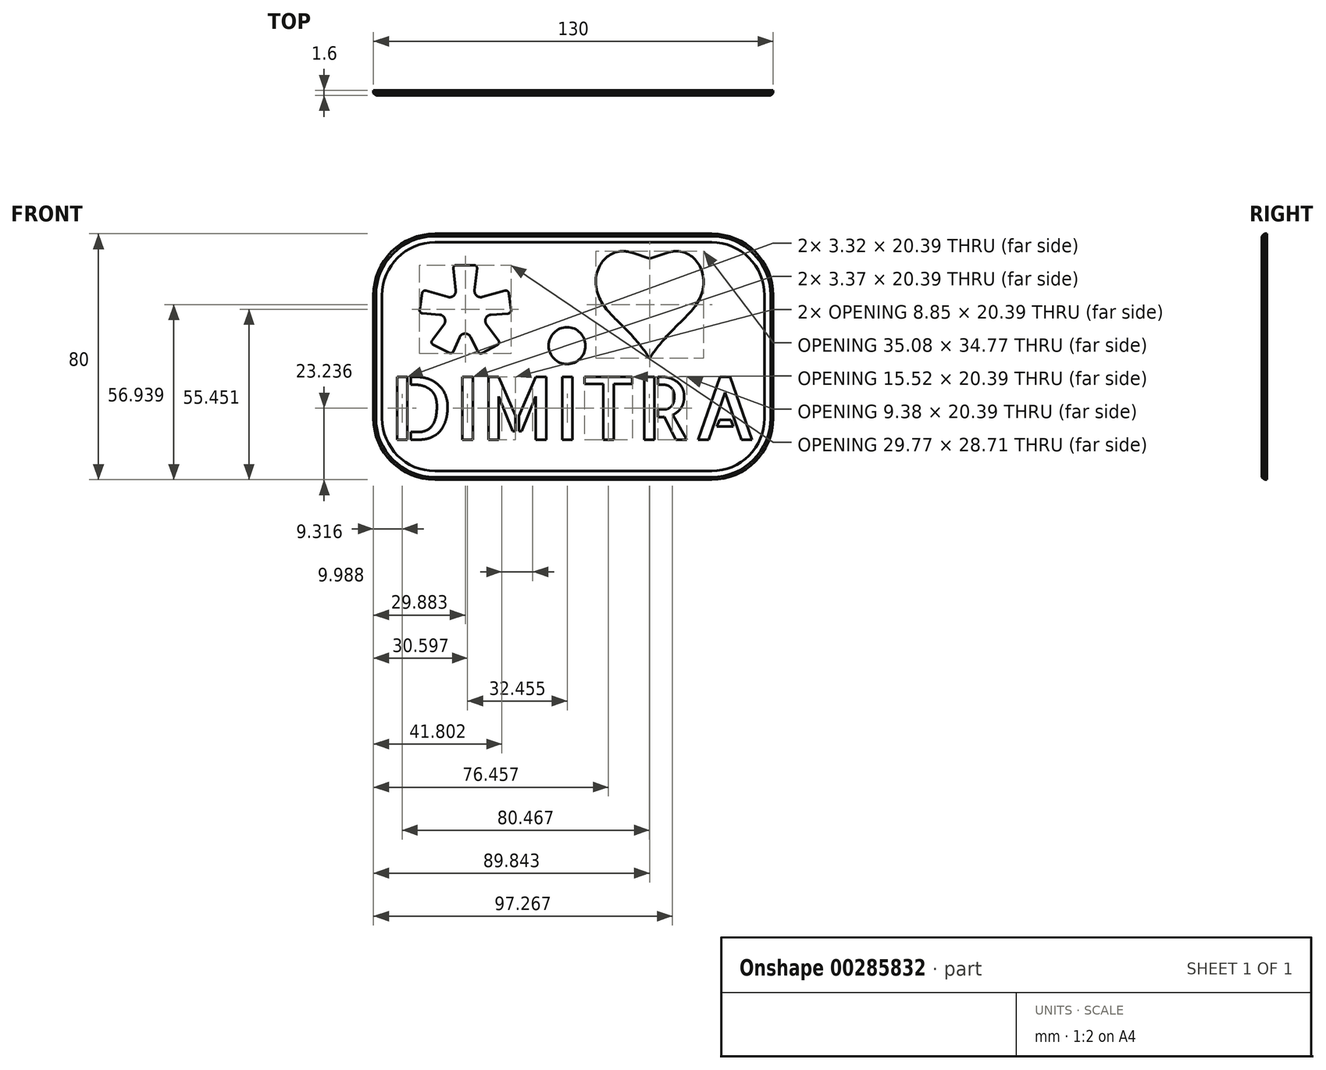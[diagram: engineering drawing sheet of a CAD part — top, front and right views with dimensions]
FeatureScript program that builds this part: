
annotation { "Feature Type Name" : "Feature", "Feature Type Description" : "" }
export const myFeature = defineFeature(function(context is Context, id is Id, definition is map)
    precondition{}
    {
        {
            var Q0;
            Q0=qCreatedBy(makeId("Front.planeOp"),FACE);
            var sketch = newSketch(context, id + "F0", { "sketchPlane" : qUnion([Q0])});
            skLineSegment(sketch, "E0.bottom", {"start": v(-65, 60) * mm, "end": v(65, 60) * mm});
            skLineSegment(sketch, "E0.top", {"start": v(-65, -20) * mm, "end": v(65, -20) * mm});
            skLineSegment(sketch, "E0.left", {"start": v(-65, 60) * mm, "end": v(-65, -20) * mm});
            skLineSegment(sketch, "E0.right", {"start": v(65, 60) * mm, "end": v(65, -20) * mm});
            skSolve(sketch);
        }
        {
            var Q0;
            Q0=qSketchRegion(id+"F0",true);
            extrude(context, id + "F1", {"entities" : qUnion([Q0]), "depth" : 1.6 * mm});
        }
        {
            var Q0;
            Q0=makeQuery(id+"F1.opExtrude","CAP_FACE",FACE,{"disambiguationData":[OSD([sQuery(id+"F0.wireOp",EDGE,"E0.bottom"),sQuery(id+"F0.wireOp",EDGE,"E0.top"),sQuery(id+"F0.wireOp",EDGE,"E0.left"),sQuery(id+"F0.wireOp",EDGE,"E0.right")])],"isStart":false});
            var sketch = newSketch(context, id + "F2", { "sketchPlane" : qUnion([Q0])});
            skText(sketch, "E1", { "text": "DIMITRA", "fontName": "AllertaStencil-Regular.ttf"});
            skText(sketch, "E2", { "text": "♥", "fontName": "NotoSansCJKjp-Regular.otf"});
            skCircle(sketch, "E3", {"center": v(-2.04, 23.59) * mm, "radius": 6 * mm});
            const initialGuessF2  = {"E1": [-0.06, -0.00696, 1, 0, 0.0204], "E2": [0.00401, 0.02116, 1, 0, 0.03]};
            skSetInitialGuess(sketch, initialGuessF2);
            skSolve(sketch);
        }
        {
            var Q0;
            Q0=qSketchRegion(id+"F2",true);
            extrude(context, id + "F3", {"entities" : qUnion([Q0]), "operationType" : NewBodyOperationType.REMOVE, "endBound" : BoundingType.THROUGH_ALL, "oppositeDirection" : true, "depth" : 25 * mm});
        }
        {
            var Q0;
            Q0=makeQuery(id+"F1.opExtrude","SWEPT_EDGE",EDGE,{"disambiguationData":[OSD([sQuery(id+"F0.wireOp",EDGE,"E0.top"),sQuery(id+"F0.wireOp",EDGE,"E0.right")])]});
            var Q1;
            Q1=makeQuery(id+"F1.opExtrude","SWEPT_EDGE",EDGE,{"disambiguationData":[OSD([sQuery(id+"F0.wireOp",EDGE,"E0.bottom"),sQuery(id+"F0.wireOp",EDGE,"E0.right")])]});
            var Q2;
            Q2=makeQuery(id+"F1.opExtrude","SWEPT_EDGE",EDGE,{"disambiguationData":[OSD([sQuery(id+"F0.wireOp",EDGE,"E0.top"),sQuery(id+"F0.wireOp",EDGE,"E0.left")])]});
            var Q3;
            Q3=makeQuery(id+"F1.opExtrude","SWEPT_EDGE",EDGE,{"disambiguationData":[OSD([sQuery(id+"F0.wireOp",EDGE,"E0.bottom"),sQuery(id+"F0.wireOp",EDGE,"E0.left")])]});
            fillet(context, id + "F4", {"entities" : qUnion([Q0, Q1, Q2, Q3]), "radius" : 20 * mm, "tangentPropagation" : true, "allowEdgeOverflow" : false});
        }
        {
            var Q0;
            Q0=makeQuery(id+"F1.opExtrude","CAP_EDGE",EDGE,{"disambiguationData":[OSD([sQuery(id+"F0.wireOp",EDGE,"E0.top")])],"isStart":false});
            chamfer(context, id + "F5", {"entities" : qUnion([Q0]), "width" : 0.8 * mm, "tangentPropagation" : true});
        }
        {
            var Q0;
            Q0=makeQuery(id+"F1.opExtrude","CAP_FACE",FACE,{"disambiguationData":[OSD([sQuery(id+"F0.wireOp",EDGE,"E0.bottom"),sQuery(id+"F0.wireOp",EDGE,"E0.top"),sQuery(id+"F0.wireOp",EDGE,"E0.left"),sQuery(id+"F0.wireOp",EDGE,"E0.right")])],"isStart":false});
            var sketch = newSketch(context, id + "F6", { "sketchPlane" : qUnion([Q0])});
            skText(sketch, "E4", { "text": "*", "fontName": "OpenSans-Bold.ttf"});
            const initialGuessF6  = {"E4": [-0.05207, 0.00257, 1, 0, 0.04476]};
            skSetInitialGuess(sketch, initialGuessF6);
            skSolve(sketch);
        }
        {
            var Q0;
            Q0=qSketchRegion(id+"F6",true);
            extrude(context, id + "F7", {"entities" : qUnion([Q0]), "operationType" : NewBodyOperationType.REMOVE, "endBound" : BoundingType.THROUGH_ALL, "oppositeDirection" : true, "depth" : 25 * mm});
        }
        {
            var Q0;
            Q0=makeQuery(id+"F1.opExtrude","CAP_FACE",FACE,{"disambiguationData":[OSD([sQuery(id+"F0.wireOp",EDGE,"E0.bottom"),sQuery(id+"F0.wireOp",EDGE,"E0.top"),sQuery(id+"F0.wireOp",EDGE,"E0.left"),sQuery(id+"F0.wireOp",EDGE,"E0.right")])],"isStart":false});
            var sketch = newSketch(context, id + "F8", { "sketchPlane" : qUnion([Q0])});
            skLineSegment(sketch, "E5.0", {"start": v(62.2, 0) * mm, "end": v(62.2, 40) * mm});
            skArc(sketch, "E5.1", {"start": v(45, -17.2) * mm, "mid": v(57.16, -12.16) * mm, "end": v(62.2, 0) * mm});
            skLineSegment(sketch, "E5.2", {"start": v(-45, -17.2) * mm, "end": v(45, -17.2) * mm});
            skArc(sketch, "E6.0", {"start": v(-62.2, 0) * mm, "mid": v(-57.16, -12.16) * mm, "end": v(-45, -17.2) * mm});
            skArc(sketch, "E6.1", {"start": v(62.2, 40) * mm, "mid": v(57.16, 52.16) * mm, "end": v(45, 57.2) * mm});
            skLineSegment(sketch, "E6.2", {"start": v(45, 57.2) * mm, "end": v(-45, 57.2) * mm});
            skArc(sketch, "E6.3", {"start": v(-45, 57.2) * mm, "mid": v(-57.16, 52.16) * mm, "end": v(-62.2, 40) * mm});
            skLineSegment(sketch, "E6.4", {"start": v(-62.2, 40) * mm, "end": v(-62.2, 0) * mm});
            skSolve(sketch);
        }
        {
            var Q0;
            Q0=makeQuery(id+"F8.imprint","IMPRINT",FACE,{"disambiguationData":[TD([[makeQuery(id+"F8.imprint","IMPRINT",EDGE,{"derivedFrom":sQuery(id+"F8.wireOp",EDGE,"E5.0")}),1.0]])]});
            extrude(context, id + "F9", {"entities" : qUnion([Q0]), "operationType" : NewBodyOperationType.REMOVE, "oppositeDirection" : true, "depth" : 0.4 * mm});
        }
        {
            var Q0;
            Q0=makeQuery(id+"F9.boolean.opBoolean","COPY",FACE,{"derivedFrom":makeQuery(id+"F9.opExtrude","CAP_FACE",FACE,{"disambiguationData":[OSD([sQuery(id+"F2.wireOp",EDGE,"E1.sketch_text.stroke-0"),sQuery(id+"F2.wireOp",EDGE,"E1.sketch_text.stroke-1"),sQuery(id+"F2.wireOp",EDGE,"E1.sketch_text.stroke-2"),sQuery(id+"F2.wireOp",EDGE,"E1.sketch_text.stroke-3"),sQuery(id+"F2.wireOp",EDGE,"E1.sketch_text.stroke-4"),sQuery(id+"F2.wireOp",EDGE,"E1.sketch_text.stroke-5"),sQuery(id+"F2.wireOp",EDGE,"E1.sketch_text.stroke-6"),sQuery(id+"F2.wireOp",EDGE,"E1.sketch_text.stroke-7"),sQuery(id+"F2.wireOp",EDGE,"E1.sketch_text.stroke-8"),sQuery(id+"F2.wireOp",EDGE,"E1.sketch_text.stroke-9"),sQuery(id+"F2.wireOp",EDGE,"E1.sketch_text.stroke-10"),sQuery(id+"F2.wireOp",EDGE,"E1.sketch_text.stroke-11"),sQuery(id+"F2.wireOp",EDGE,"E1.sketch_text.stroke-12"),sQuery(id+"F2.wireOp",EDGE,"E1.sketch_text.stroke-13"),sQuery(id+"F2.wireOp",EDGE,"E1.sketch_text.stroke-14"),sQuery(id+"F2.wireOp",EDGE,"E1.sketch_text.stroke-15"),sQuery(id+"F2.wireOp",EDGE,"E1.sketch_text.stroke-16"),sQuery(id+"F2.wireOp",EDGE,"E1.sketch_text.stroke-17"),sQuery(id+"F2.wireOp",EDGE,"E1.sketch_text.stroke-18"),sQuery(id+"F2.wireOp",EDGE,"E1.sketch_text.stroke-19"),sQuery(id+"F2.wireOp",EDGE,"E1.sketch_text.stroke-20"),sQuery(id+"F2.wireOp",EDGE,"E1.sketch_text.stroke-21"),sQuery(id+"F2.wireOp",EDGE,"E1.sketch_text.stroke-22"),sQuery(id+"F2.wireOp",EDGE,"E1.sketch_text.stroke-23"),sQuery(id+"F2.wireOp",EDGE,"E1.sketch_text.stroke-24"),sQuery(id+"F2.wireOp",EDGE,"E1.sketch_text.stroke-25"),sQuery(id+"F2.wireOp",EDGE,"E1.sketch_text.stroke-26"),sQuery(id+"F2.wireOp",EDGE,"E1.sketch_text.stroke-27"),sQuery(id+"F2.wireOp",EDGE,"E1.sketch_text.stroke-28"),sQuery(id+"F2.wireOp",EDGE,"E1.sketch_text.stroke-29"),sQuery(id+"F2.wireOp",EDGE,"E1.sketch_text.stroke-30"),sQuery(id+"F2.wireOp",EDGE,"E1.sketch_text.stroke-31"),sQuery(id+"F2.wireOp",EDGE,"E1.sketch_text.stroke-32"),sQuery(id+"F2.wireOp",EDGE,"E1.sketch_text.stroke-33"),sQuery(id+"F2.wireOp",EDGE,"E1.sketch_text.stroke-34"),sQuery(id+"F2.wireOp",EDGE,"E1.sketch_text.stroke-35"),sQuery(id+"F2.wireOp",EDGE,"E1.sketch_text.stroke-36"),sQuery(id+"F2.wireOp",EDGE,"E1.sketch_text.stroke-37"),sQuery(id+"F2.wireOp",EDGE,"E1.sketch_text.stroke-38"),sQuery(id+"F2.wireOp",EDGE,"E1.sketch_text.stroke-39"),sQuery(id+"F2.wireOp",EDGE,"E1.sketch_text.stroke-40"),sQuery(id+"F2.wireOp",EDGE,"E1.sketch_text.stroke-41"),sQuery(id+"F2.wireOp",EDGE,"E1.sketch_text.stroke-42"),sQuery(id+"F2.wireOp",EDGE,"E1.sketch_text.stroke-43"),sQuery(id+"F2.wireOp",EDGE,"E1.sketch_text.stroke-44"),sQuery(id+"F2.wireOp",EDGE,"E1.sketch_text.stroke-45"),sQuery(id+"F2.wireOp",EDGE,"E1.sketch_text.stroke-46"),sQuery(id+"F2.wireOp",EDGE,"E1.sketch_text.stroke-47"),sQuery(id+"F2.wireOp",EDGE,"E1.sketch_text.stroke-48"),sQuery(id+"F2.wireOp",EDGE,"E1.sketch_text.stroke-49"),sQuery(id+"F2.wireOp",EDGE,"E1.sketch_text.stroke-50"),sQuery(id+"F2.wireOp",EDGE,"E1.sketch_text.stroke-51"),sQuery(id+"F2.wireOp",EDGE,"E1.sketch_text.stroke-52"),sQuery(id+"F2.wireOp",EDGE,"E1.sketch_text.stroke-53"),sQuery(id+"F2.wireOp",EDGE,"E1.sketch_text.stroke-54"),sQuery(id+"F2.wireOp",EDGE,"E1.sketch_text.stroke-55"),sQuery(id+"F2.wireOp",EDGE,"E1.sketch_text.stroke-56"),sQuery(id+"F2.wireOp",EDGE,"E1.sketch_text.stroke-57"),sQuery(id+"F2.wireOp",EDGE,"E1.sketch_text.stroke-58"),sQuery(id+"F2.wireOp",EDGE,"E1.sketch_text.stroke-59"),sQuery(id+"F2.wireOp",EDGE,"E1.sketch_text.stroke-60"),sQuery(id+"F2.wireOp",EDGE,"E1.sketch_text.stroke-61"),sQuery(id+"F2.wireOp",EDGE,"E1.sketch_text.stroke-62"),sQuery(id+"F2.wireOp",EDGE,"E1.sketch_text.stroke-63"),sQuery(id+"F2.wireOp",EDGE,"E1.sketch_text.stroke-64"),sQuery(id+"F2.wireOp",EDGE,"E1.sketch_text.stroke-65"),sQuery(id+"F2.wireOp",EDGE,"E1.sketch_text.stroke-66"),sQuery(id+"F2.wireOp",EDGE,"E1.sketch_text.stroke-67"),sQuery(id+"F2.wireOp",EDGE,"E1.sketch_text.stroke-68"),sQuery(id+"F2.wireOp",EDGE,"E1.sketch_text.stroke-69"),sQuery(id+"F2.wireOp",EDGE,"E1.sketch_text.stroke-70"),sQuery(id+"F2.wireOp",EDGE,"E1.sketch_text.stroke-71"),sQuery(id+"F2.wireOp",EDGE,"E1.sketch_text.stroke-72"),sQuery(id+"F2.wireOp",EDGE,"E1.sketch_text.stroke-73"),sQuery(id+"F2.wireOp",EDGE,"E1.sketch_text.stroke-74"),sQuery(id+"F2.wireOp",EDGE,"E1.sketch_text.stroke-75"),sQuery(id+"F2.wireOp",EDGE,"E1.sketch_text.stroke-76"),sQuery(id+"F2.wireOp",EDGE,"E1.sketch_text.stroke-77"),sQuery(id+"F2.wireOp",EDGE,"E1.sketch_text.stroke-78"),sQuery(id+"F2.wireOp",EDGE,"E1.sketch_text.stroke-79"),sQuery(id+"F2.wireOp",EDGE,"E1.sketch_text.stroke-80"),sQuery(id+"F2.wireOp",EDGE,"E1.sketch_text.stroke-81"),sQuery(id+"F2.wireOp",EDGE,"E1.sketch_text.stroke-82"),sQuery(id+"F2.wireOp",EDGE,"E1.sketch_text.stroke-83"),sQuery(id+"F2.wireOp",EDGE,"E1.sketch_text.stroke-84"),sQuery(id+"F2.wireOp",EDGE,"E1.sketch_text.stroke-85"),sQuery(id+"F2.wireOp",EDGE,"E1.sketch_text.stroke-86"),sQuery(id+"F2.wireOp",EDGE,"E1.sketch_text.stroke-87"),sQuery(id+"F2.wireOp",EDGE,"E1.sketch_text.stroke-88"),sQuery(id+"F2.wireOp",EDGE,"E1.sketch_text.stroke-89"),sQuery(id+"F2.wireOp",EDGE,"E1.sketch_text.stroke-90"),sQuery(id+"F2.wireOp",EDGE,"E1.sketch_text.stroke-91"),sQuery(id+"F2.wireOp",EDGE,"E1.sketch_text.stroke-92"),sQuery(id+"F2.wireOp",EDGE,"E1.sketch_text.stroke-93"),sQuery(id+"F2.wireOp",EDGE,"E1.sketch_text.stroke-94"),sQuery(id+"F2.wireOp",EDGE,"E1.sketch_text.stroke-95"),sQuery(id+"F2.wireOp",EDGE,"E1.sketch_text.stroke-96"),sQuery(id+"F2.wireOp",EDGE,"E1.sketch_text.stroke-97"),sQuery(id+"F2.wireOp",EDGE,"E1.sketch_text.stroke-98"),sQuery(id+"F2.wireOp",EDGE,"E2.sketch_text.stroke-0"),sQuery(id+"F2.wireOp",EDGE,"E2.sketch_text.stroke-1"),sQuery(id+"F2.wireOp",EDGE,"E2.sketch_text.stroke-2"),sQuery(id+"F2.wireOp",EDGE,"E2.sketch_text.stroke-3"),sQuery(id+"F2.wireOp",EDGE,"E2.sketch_text.stroke-4"),sQuery(id+"F2.wireOp",EDGE,"E2.sketch_text.stroke-5"),sQuery(id+"F2.wireOp",EDGE,"E2.sketch_text.stroke-6"),sQuery(id+"F2.wireOp",EDGE,"E2.sketch_text.stroke-7"),sQuery(id+"F2.wireOp",EDGE,"E2.sketch_text.stroke-8"),sQuery(id+"F2.wireOp",EDGE,"E2.sketch_text.stroke-9"),sQuery(id+"F2.wireOp",EDGE,"E2.sketch_text.stroke-10"),sQuery(id+"F6.wireOp",EDGE,"E4.sketch_text.stroke-0"),sQuery(id+"F6.wireOp",EDGE,"E4.sketch_text.stroke-1"),sQuery(id+"F6.wireOp",EDGE,"E4.sketch_text.stroke-2"),sQuery(id+"F6.wireOp",EDGE,"E4.sketch_text.stroke-3"),sQuery(id+"F6.wireOp",EDGE,"E4.sketch_text.stroke-4"),sQuery(id+"F6.wireOp",EDGE,"E4.sketch_text.stroke-5"),sQuery(id+"F6.wireOp",EDGE,"E4.sketch_text.stroke-6"),sQuery(id+"F6.wireOp",EDGE,"E4.sketch_text.stroke-7"),sQuery(id+"F6.wireOp",EDGE,"E4.sketch_text.stroke-8"),sQuery(id+"F6.wireOp",EDGE,"E4.sketch_text.stroke-9"),sQuery(id+"F6.wireOp",EDGE,"E4.sketch_text.stroke-10"),sQuery(id+"F6.wireOp",EDGE,"E4.sketch_text.stroke-11"),sQuery(id+"F6.wireOp",EDGE,"E4.sketch_text.stroke-12"),sQuery(id+"F6.wireOp",EDGE,"E4.sketch_text.stroke-13"),sQuery(id+"F6.wireOp",EDGE,"E4.sketch_text.stroke-14"),sQuery(id+"F6.wireOp",EDGE,"E4.sketch_text.stroke-15"),sQuery(id+"F6.wireOp",EDGE,"E4.sketch_text.stroke-16"),sQuery(id+"F6.wireOp",EDGE,"E4.sketch_text.stroke-17"),sQuery(id+"F6.wireOp",EDGE,"E4.sketch_text.stroke-18"),sQuery(id+"F6.wireOp",EDGE,"E4.sketch_text.stroke-19"),sQuery(id+"F6.wireOp",EDGE,"E4.sketch_text.stroke-20"),sQuery(id+"F6.wireOp",EDGE,"E4.sketch_text.stroke-21"),sQuery(id+"F6.wireOp",EDGE,"E4.sketch_text.stroke-22"),sQuery(id+"F6.wireOp",EDGE,"E4.sketch_text.stroke-23"),sQuery(id+"F6.wireOp",EDGE,"E4.sketch_text.stroke-24"),sQuery(id+"F6.wireOp",EDGE,"E4.sketch_text.stroke-25"),sQuery(id+"F6.wireOp",EDGE,"E4.sketch_text.stroke-26"),sQuery(id+"F6.wireOp",EDGE,"E4.sketch_text.stroke-27"),sQuery(id+"F6.wireOp",EDGE,"E4.sketch_text.stroke-28"),sQuery(id+"F6.wireOp",EDGE,"E4.sketch_text.stroke-29"),sQuery(id+"F6.wireOp",EDGE,"E4.sketch_text.stroke-30"),sQuery(id+"F6.wireOp",EDGE,"E4.sketch_text.stroke-31"),sQuery(id+"F6.wireOp",EDGE,"E4.sketch_text.stroke-32"),sQuery(id+"F6.wireOp",EDGE,"E4.sketch_text.stroke-33"),sQuery(id+"F8.wireOp",EDGE,"E5.0"),sQuery(id+"F8.wireOp",EDGE,"E5.1"),sQuery(id+"F8.wireOp",EDGE,"E5.2"),sQuery(id+"F8.wireOp",EDGE,"E6.0"),sQuery(id+"F8.wireOp",EDGE,"E6.1"),sQuery(id+"F8.wireOp",EDGE,"E6.2"),sQuery(id+"F8.wireOp",EDGE,"E6.3"),sQuery(id+"F8.wireOp",EDGE,"E6.4")])],"isStart":false})});
            var sketch = newSketch(context, id + "F10", { "sketchPlane" : qUnion([Q0])});
            skLineSegment(sketch, "E7", {"start": v(20.28, 45.7) * mm, "end": v(30.45, 45.7) * mm});
            skLineSegment(sketch, "E8", {"start": v(30.45, 45.7) * mm, "end": v(30.45, 53.8) * mm});
            skLineSegment(sketch, "E9", {"start": v(30.45, 53.8) * mm, "end": v(24.85, 51.87) * mm});
            skLineSegment(sketch, "E10", {"start": v(24.85, 51.87) * mm, "end": v(19.22, 53.8) * mm});
            skLineSegment(sketch, "E11", {"start": v(19.22, 53.8) * mm, "end": v(19.22, 45.6) * mm});
            skLineSegment(sketch, "E12", {"start": v(19.22, 45.6) * mm, "end": v(20.28, 45.7) * mm});
            skSolve(sketch);
        }
        {
            var Q0;
            Q0 = qSketchRegion(id + "F10", true);
            extrude(context, id + "F11", {"entities" : qUnion([Q0]), "operationType" : NewBodyOperationType.REMOVE, "oppositeDirection" : true, "depth" : 25 * mm});
        }
        {
            var Q0;
            Q0=makeQuery(id+"F7.boolean.opBoolean","COPY",EDGE,{"derivedFrom":makeQuery(id+"F7.opExtrude","SWEPT_EDGE",EDGE,{"disambiguationData":[OSD([sQuery(id+"F6.wireOp",EDGE,"E4.sketch_text.stroke-6"),sQuery(id+"F6.wireOp",EDGE,"E4.sketch_text.stroke-7")])]})});
            var Q1;
            Q1=makeQuery(id+"F7.boolean.opBoolean","COPY",EDGE,{"derivedFrom":makeQuery(id+"F7.opExtrude","SWEPT_EDGE",EDGE,{"disambiguationData":[OSD([sQuery(id+"F6.wireOp",EDGE,"E4.sketch_text.stroke-9"),sQuery(id+"F6.wireOp",EDGE,"E4.sketch_text.stroke-10")])]})});
            var Q2;
            Q2=makeQuery(id+"F7.boolean.opBoolean","COPY",EDGE,{"derivedFrom":makeQuery(id+"F7.opExtrude","SWEPT_EDGE",EDGE,{"disambiguationData":[OSD([sQuery(id+"F6.wireOp",EDGE,"E4.sketch_text.stroke-3"),sQuery(id+"F6.wireOp",EDGE,"E4.sketch_text.stroke-4")])]})});
            var Q3;
            Q3=makeQuery(id+"F7.boolean.opBoolean","COPY",EDGE,{"derivedFrom":makeQuery(id+"F7.opExtrude","SWEPT_EDGE",EDGE,{"disambiguationData":[OSD([sQuery(id+"F6.wireOp",EDGE,"E4.sketch_text.stroke-12"),sQuery(id+"F6.wireOp",EDGE,"E4.sketch_text.stroke-13")])]})});
            var Q4;
            Q4=makeQuery(id+"F7.boolean.opBoolean","COPY",EDGE,{"derivedFrom":makeQuery(id+"F7.opExtrude","SWEPT_EDGE",EDGE,{"disambiguationData":[OSD([sQuery(id+"F6.wireOp",EDGE,"E4.sketch_text.stroke-0"),sQuery(id+"F6.wireOp",EDGE,"E4.sketch_text.stroke-1")])]})});
            fillet(context, id + "F12", {"entities" : qUnion([Q0, Q1, Q2, Q3, Q4]), "radius" : 2 * mm, "tangentPropagation" : true, "allowEdgeOverflow" : false});
        }
        {
            var Q0;
            Q0=makeQuery(id+"F7.boolean.opBoolean","COPY",EDGE,{"derivedFrom":makeQuery(id+"F7.opExtrude","SWEPT_EDGE",EDGE,{"disambiguationData":[OSD([sQuery(id+"F6.wireOp",EDGE,"E4.sketch_text.stroke-0"),sQuery(id+"F6.wireOp",EDGE,"E4.sketch_text.stroke-14")])]})});
            var Q1;
            Q1=makeQuery(id+"F7.boolean.opBoolean","COPY",EDGE,{"derivedFrom":makeQuery(id+"F7.opExtrude","SWEPT_EDGE",EDGE,{"disambiguationData":[OSD([sQuery(id+"F6.wireOp",EDGE,"E4.sketch_text.stroke-1"),sQuery(id+"F6.wireOp",EDGE,"E4.sketch_text.stroke-2")])]})});
            var Q2;
            Q2=makeQuery(id+"F7.boolean.opBoolean","COPY",EDGE,{"derivedFrom":makeQuery(id+"F7.opExtrude","SWEPT_EDGE",EDGE,{"disambiguationData":[OSD([sQuery(id+"F6.wireOp",EDGE,"E4.sketch_text.stroke-13"),sQuery(id+"F6.wireOp",EDGE,"E4.sketch_text.stroke-14")])]})});
            var Q3;
            Q3=makeQuery(id+"F7.boolean.opBoolean","COPY",EDGE,{"derivedFrom":makeQuery(id+"F7.opExtrude","SWEPT_EDGE",EDGE,{"disambiguationData":[OSD([sQuery(id+"F6.wireOp",EDGE,"E4.sketch_text.stroke-11"),sQuery(id+"F6.wireOp",EDGE,"E4.sketch_text.stroke-12")])]})});
            var Q4;
            Q4=makeQuery(id+"F7.boolean.opBoolean","COPY",EDGE,{"derivedFrom":makeQuery(id+"F7.opExtrude","SWEPT_EDGE",EDGE,{"disambiguationData":[OSD([sQuery(id+"F6.wireOp",EDGE,"E4.sketch_text.stroke-10"),sQuery(id+"F6.wireOp",EDGE,"E4.sketch_text.stroke-11")])]})});
            var Q5;
            Q5=makeQuery(id+"F7.boolean.opBoolean","COPY",EDGE,{"derivedFrom":makeQuery(id+"F7.opExtrude","SWEPT_EDGE",EDGE,{"disambiguationData":[OSD([sQuery(id+"F6.wireOp",EDGE,"E4.sketch_text.stroke-8"),sQuery(id+"F6.wireOp",EDGE,"E4.sketch_text.stroke-9")])]})});
            var Q6;
            Q6=makeQuery(id+"F7.boolean.opBoolean","COPY",EDGE,{"derivedFrom":makeQuery(id+"F7.opExtrude","SWEPT_EDGE",EDGE,{"disambiguationData":[OSD([sQuery(id+"F6.wireOp",EDGE,"E4.sketch_text.stroke-5"),sQuery(id+"F6.wireOp",EDGE,"E4.sketch_text.stroke-6")])]})});
            var Q7;
            Q7=makeQuery(id+"F7.boolean.opBoolean","COPY",EDGE,{"derivedFrom":makeQuery(id+"F7.opExtrude","SWEPT_EDGE",EDGE,{"disambiguationData":[OSD([sQuery(id+"F6.wireOp",EDGE,"E4.sketch_text.stroke-7"),sQuery(id+"F6.wireOp",EDGE,"E4.sketch_text.stroke-8")])]})});
            var Q8;
            Q8=makeQuery(id+"F7.boolean.opBoolean","COPY",EDGE,{"derivedFrom":makeQuery(id+"F7.opExtrude","SWEPT_EDGE",EDGE,{"disambiguationData":[OSD([sQuery(id+"F6.wireOp",EDGE,"E4.sketch_text.stroke-2"),sQuery(id+"F6.wireOp",EDGE,"E4.sketch_text.stroke-3")])]})});
            var Q9;
            Q9=makeQuery(id+"F7.boolean.opBoolean","COPY",EDGE,{"derivedFrom":makeQuery(id+"F7.opExtrude","SWEPT_EDGE",EDGE,{"disambiguationData":[OSD([sQuery(id+"F6.wireOp",EDGE,"E4.sketch_text.stroke-4"),sQuery(id+"F6.wireOp",EDGE,"E4.sketch_text.stroke-5")])]})});
            fillet(context, id + "F13", {"entities" : qUnion([Q0, Q1, Q2, Q3, Q4, Q5, Q6, Q7, Q8, Q9]), "radius" : 1 * mm, "tangentPropagation" : true, "allowEdgeOverflow" : false});
        }
    });
